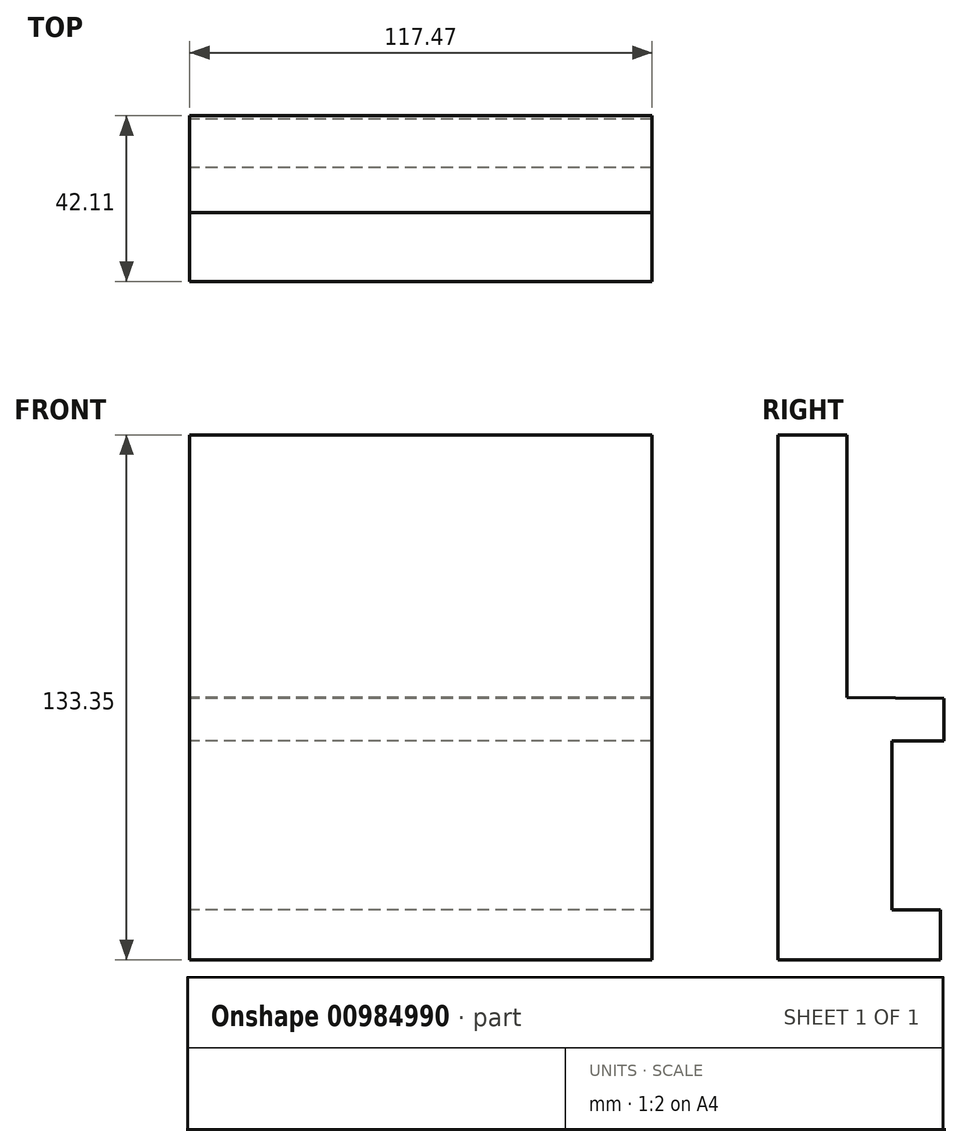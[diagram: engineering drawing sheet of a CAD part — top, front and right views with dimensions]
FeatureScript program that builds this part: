
annotation { "Feature Type Name" : "Feature", "Feature Type Description" : "" }
export const myFeature = defineFeature(function(context is Context, id is Id, definition is map)
    precondition{}
    {
        {
            var Q0;
            Q0=qCreatedBy(makeId("Right.planeOp"),FACE);
            var sketch = newSketch(context, id + "F0", { "sketchPlane" : qUnion([Q0])});
            skLineSegment(sketch, "E0", {"start": v(-53.4, 73.13) * mm, "end": v(-53.4, -60.22) * mm});
            skLineSegment(sketch, "E1", {"start": v(-53.4, 73.13) * mm, "end": v(-35.93, 73.13) * mm});
            skLineSegment(sketch, "E2", {"start": v(-35.93, 73.13) * mm, "end": v(-35.93, 6.45) * mm});
            skLineSegment(sketch, "E3", {"start": v(-53.4, -60.22) * mm, "end": v(-12.12, -60.22) * mm});
            skLineSegment(sketch, "E4", {"start": v(-12.12, -60.22) * mm, "end": v(-12.12, -47.52) * mm});
            skLineSegment(sketch, "E5", {"start": v(-12.12, -47.52) * mm, "end": v(-24.51, -47.52) * mm});
            skLineSegment(sketch, "E6", {"start": v(-24.51, -47.52) * mm, "end": v(-24.51, -4.66) * mm});
            skLineSegment(sketch, "E7", {"start": v(-24.51, -4.66) * mm, "end": v(-13.4, -4.66) * mm});
            skLineSegment(sketch, "E8", {"start": v(-13.4, -4.66) * mm, "end": v(-11.28, -4.66) * mm});
            skLineSegment(sketch, "E9", {"start": v(-11.28, -4.66) * mm, "end": v(-11.28, 6.17) * mm});
            skLineSegment(sketch, "E10", {"start": v(-11.28, 6.17) * mm, "end": v(-35.93, 6.45) * mm});
            skSolve(sketch);
        }
        {
            var Q0;
            Q0 = qSketchRegion(id + "F0", true);
            extrude(context, id + "F1", {"entities" : qUnion([Q0]), "depth" : 117.47 * mm, "offsetDistance" : 25.4 * mm});
        }
    });
